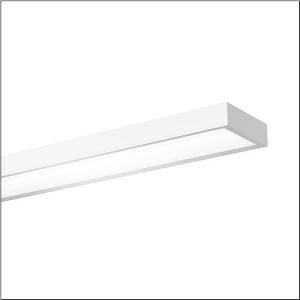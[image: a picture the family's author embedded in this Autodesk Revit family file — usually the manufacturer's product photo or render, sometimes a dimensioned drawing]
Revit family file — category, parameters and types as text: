
# Revit family: sport_31_51hs12dc3dca
name_source: partatom
category: Lighting Fixtures
units: mm (PartAtom-declared; Revit-internal decimal feet)

## family parameters
Cut with Voids When Loaded = No
Host = Face
Light Source = No
Part Type = Normal
Room Calculation Point = No
Round Connector Dimension = Use Diameter
Shared = No

## types (1)
- --- (1 x LED, 7500 lm, 55.4 W, 3000K)
    Apparent Load = 55 VA
    CIE Flux Codes = 65 89 97 100 100
    Color Rendering = 80
    Color Temperature = 3000K
    Default Elevation = 1800 mm
    Description = Sport 31, LED high bay luminaire, primary light control with reflector, of sheet steel, primary anti-glare with prismatic structure, of PC, primary optical cover: cover panel, of PC, light emission: direct distribution, primary light characteristic: symmetric, installation type: suspended mounting, recessed, surface-mounted, LED, rated luminous flux: 7.500lm, luminous efficacy: 130lm/W, light colour: 830, colour temperature: 3000K, control gear: ECG DALI, with terminal, 5-pole, max. 2.5mm², mains connection: 220..240V, AC/DC, 50/60Hz, rated input power: 58W, housing, of sheet steel, traffic white (RAL 9016), length: 1.540mm, width: 315mm, height: 95mm, protection rating (complete): IP20, protection rating (lamp compartment, on room side): IP50, insulation class (complete): insulation class I (protective earthing), certification: CE, ENEC, UKCA, ball protection: ball impact resistant with ceiling mounting or chain suspension, impact resistance: IK08, permissible operating ambient temperature: -20..+35°C, standard: DIN 18032-3, EN 60598-2-22, packaging unit: 1 piece
    Height = 100 mm  [stored 0.328084 ft]
    Lamp = 1 x LED
    Lamp Light Flux = 7500 lm
    Lamp Power = 55.4 W
    Lamp count = 1
    Length = 1500 mm
    Luminous efficacy = 135 lm/W
    Manufacturer = Siteco
    ModVariant = No
    Model = 51HS12DC3DCA
    Mounting Place = Ceiling
    Mounting Type = Pendant
    Number of Poles = 1
    OnlyDefault = Yes
    Power Factor = 1
    Product Name = Sport 31
    Product group = LED high bay luminaire
    ProductGroupID = 903
    Protection Class = Protection class I
    Protection Degree = IP 20
    RLX_Detail_Level = 1
    RLX_Emergency_Light_Flux = 0 lm
    RLX_Emergency_Type = 0
    RLX_Emergency_Type_DB = No
    RlxData = <blob elided: 22769 chars, md5=59443e4a>
    Socket = socket
    Standby Power = 0 W
    System Light Flux = 7500 lm
    System Power = 55 W
    Type Comments = factory setting: luminous flux: 100 % | dim-lin: 254 | 234 mA
    Type Image = l_1006823.jpg
    URL = http://relux.com
    VarID = @adj_133129
    Voltage = 0 V
    Weight = 0.00 kg
    Width = 315 mm

note: [stored X ft] marks values corroborated as IEEE doubles in the binary element streams (Revit-internal decimal feet)

## geometry (parser evidence)
native form markers: Blend x4, Sweep x11
no freeform markers — native parametric forms only
